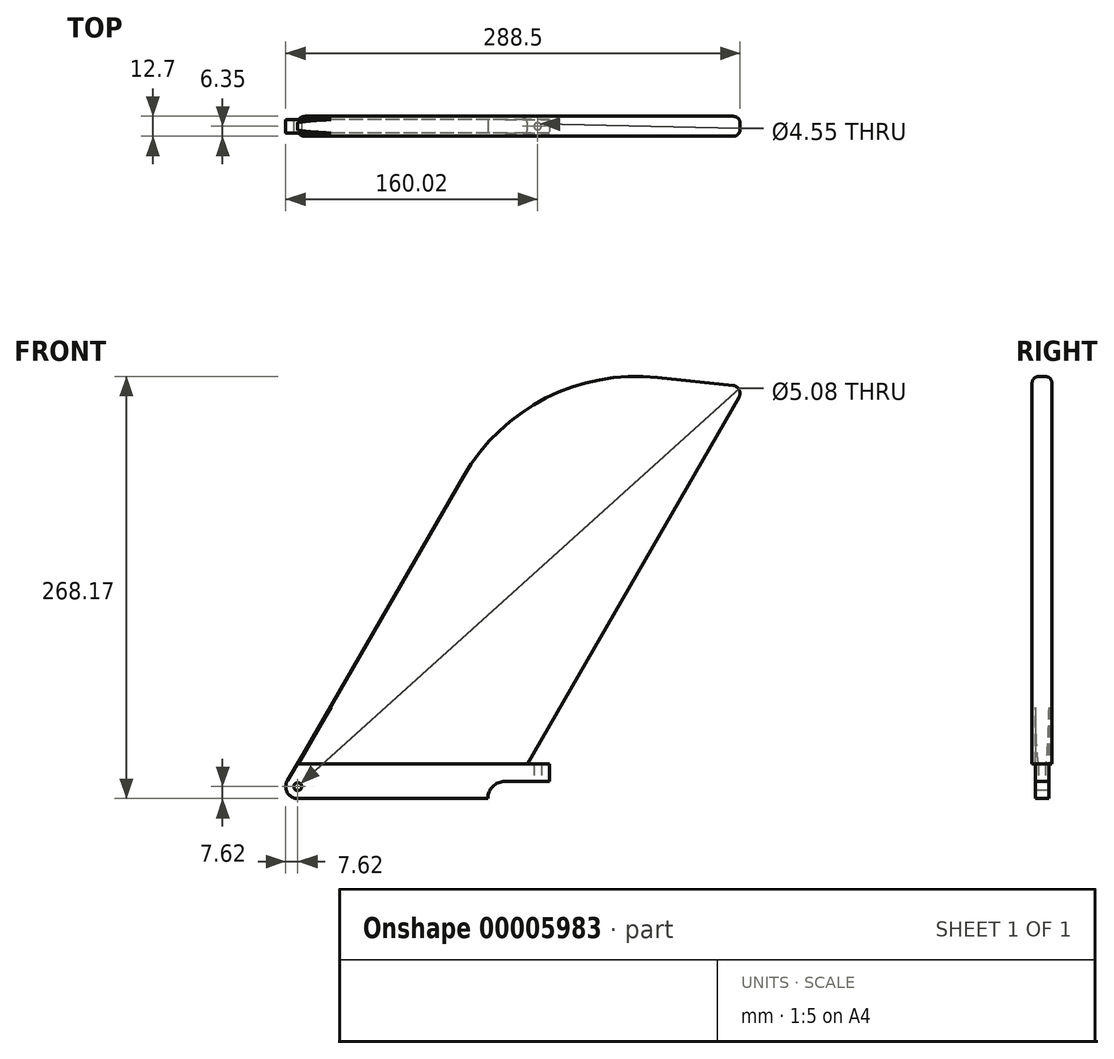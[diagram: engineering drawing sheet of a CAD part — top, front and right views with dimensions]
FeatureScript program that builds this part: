
annotation { "Feature Type Name" : "Feature", "Feature Type Description" : "" }
export const myFeature = defineFeature(function(context is Context, id is Id, definition is map)
    precondition{}
    {
        {
            var Q0;
            Q0=qCreatedBy(makeId("Top.planeOp"),FACE);
            var sketch = newSketch(context, id + "F0", { "sketchPlane" : qUnion([Q0])});
            skLineSegment(sketch, "E0.rect.bottom", {"start": v(83.82, 4.25) * mm, "end": v(-83.82, 4.25) * mm});
            skLineSegment(sketch, "E0.rect.top", {"start": v(83.82, -4.25) * mm, "end": v(-83.82, -4.25) * mm});
            skLineSegment(sketch, "E0.rect.left", {"start": v(83.82, 4.25) * mm, "end": v(83.82, -4.25) * mm});
            skLineSegment(sketch, "E0.rect.right", {"start": v(-83.82, 4.25) * mm, "end": v(-83.82, -4.25) * mm});
            skPoint(sketch, "E0.rect.middle", {"position": v(0, 0) * mm});
            skSolve(sketch);
        }
        {
            var Q0;
            Q0 = qSketchRegion(id + "F0", true);
            extrude(context, id + "F1", {"entities" : qUnion([Q0]), "depth" : 22.1 * mm});
        }
        {
            var Q0;
            Q0=qCreatedBy(makeId("Front.planeOp"),FACE);
            var sketch = newSketch(context, id + "F2", { "sketchPlane" : qUnion([Q0])});
            skArc(sketch, "E1", {"start": v(55.37, 10.85) * mm, "mid": v(47.7, 7.67) * mm, "end": v(44.52, 0) * mm});
            skLineSegment(sketch, "E2.0", {"start": v(83.82, 22.1) * mm, "end": v(83.82, 0) * mm});
            skLineSegment(sketch, "E3", {"start": v(55.37, 10.85) * mm, "end": v(83.82, 10.85) * mm});
            skLineSegment(sketch, "E4.0", {"start": v(83.82, 0) * mm, "end": v(-83.82, 0) * mm});
            skSolve(sketch);
        }
        {
            var Q0;
            Q0 = qSketchRegion(id + "F2", true);
            extrude(context, id + "F3", {"entities" : qUnion([Q0]), "operationType" : NewBodyOperationType.REMOVE, "endBound" : BoundingType.SYMMETRIC, "oppositeDirection" : true, "depth" : 25.4 * mm});
        }
        {
            var Q0;
            Q0=qCreatedBy(makeId("Front.planeOp"),FACE);
            var sketch = newSketch(context, id + "F4", { "sketchPlane" : qUnion([Q0])});
            skCircle(sketch, "E5", {"center": v(-76.2, 7.62) * mm, "radius": 2.54 * mm});
            skLineSegment(sketch, "E6.0", {"start": v(-83.82, 22.1) * mm, "end": v(-83.82, 0) * mm});
            skLineSegment(sketch, "E7.0", {"start": v(44.52, 0) * mm, "end": v(-83.82, 0) * mm});
            skSolve(sketch);
        }
        {
            var Q0;
            Q0=makeQuery(id+"F4.imprint","IMPRINT",FACE,{"disambiguationData":[TD([[makeQuery(id+"F4.imprint","IMPRINT",EDGE,{"derivedFrom":sQuery(id+"F4.wireOp",EDGE,"E5")}),1.0]])]});
            extrude(context, id + "F5", {"entities" : qUnion([Q0]), "operationType" : NewBodyOperationType.REMOVE, "endBound" : BoundingType.SYMMETRIC, "oppositeDirection" : true, "depth" : 25.4 * mm});
        }
        {
            var Q0;
            Q0=qCreatedBy(makeId("Front.planeOp"),FACE);
            var sketch = newSketch(context, id + "F6", { "sketchPlane" : qUnion([Q0])});
            skCircle(sketch, "E8.0", {"center": v(-76.2, 7.62) * mm, "radius": 2.54 * mm});
            skLineSegment(sketch, "E9.0", {"start": v(44.52, 0) * mm, "end": v(-83.82, 0) * mm});
            skLineSegment(sketch, "E10.0", {"start": v(-83.82, 22.1) * mm, "end": v(-83.82, 0) * mm});
            skArc(sketch, "E11", {"start": v(-82.74, 11.53) * mm, "mid": v(-82.83, 3.86) * mm, "end": v(-76.2, 0) * mm});
            skLineSegment(sketch, "E12", {"start": v(-76.32, 22.28) * mm, "end": v(-82.74, 11.53) * mm});
            skLineSegment(sketch, "E13", {"start": v(-76.32, 22.28) * mm, "end": v(-83.82, 22.1) * mm});
            skLineSegment(sketch, "E14", {"start": v(-83.82, 0) * mm, "end": v(-76.2, 0) * mm});
            skSolve(sketch);
        }
        {
            var Q0;
            Q0 = qSketchRegion(id + "F6", true);
            extrude(context, id + "F7", {"entities" : qUnion([Q0]), "operationType" : NewBodyOperationType.REMOVE, "endBound" : BoundingType.SYMMETRIC, "oppositeDirection" : true, "depth" : 25.4 * mm});
        }
        {
            var Q0;
            Q0=makeQuery(id+"F3.boolean.opBoolean","COPY",FACE,{"derivedFrom":makeQuery(id+"F3.opExtrude","SWEPT_FACE",FACE,{"disambiguationData":[OSD([sQuery(id+"F2.wireOp",EDGE,"E3")])]})});
            var sketch = newSketch(context, id + "F8", { "sketchPlane" : qUnion([Q0])});
            skCircle(sketch, "E15", {"center": v(76.2, 0) * mm, "radius": 2.27 * mm});
            skSolve(sketch);
        }
        {
            var Q0;
            Q0 = qSketchRegion(id + "F8", true);
            extrude(context, id + "F9", {"entities" : qUnion([Q0]), "operationType" : NewBodyOperationType.REMOVE, "oppositeDirection" : true, "depth" : 25.4 * mm});
        }
        {
            var Q0;
            Q0=qCreatedBy(makeId("Front.planeOp"),FACE);
            var sketch = newSketch(context, id + "F10", { "sketchPlane" : qUnion([Q0])});
            skPoint(sketch, "E16.0", {"position": v(-76.43, 22.1) * mm});
            skLineSegment(sketch, "E17.0", {"start": v(83.82, 22.1) * mm, "end": v(-76.43, 22.1) * mm});
            skLineSegment(sketch, "E18", {"start": v(-76.43, 22.1) * mm, "end": v(70.22, 276.1) * mm});
            skLineSegment(sketch, "E19", {"start": v(70.22, 276.1) * mm, "end": v(207.91, 261.63) * mm});
            skLineSegment(sketch, "E20", {"start": v(207.91, 261.63) * mm, "end": v(69.62, 22.1) * mm});
            skSolve(sketch);
        }
        {
            var Q0;
            Q0 = qSketchRegion(id + "F10", true);
            extrude(context, id + "F11", {"entities" : qUnion([Q0]), "operationType" : NewBodyOperationType.ADD, "endBound" : BoundingType.SYMMETRIC, "depth" : 12.7 * mm});
        }
        {
            var Q0;
            Q0=makeQuery(id+"F11.opExtrude","SWEPT_EDGE",EDGE,{"disambiguationData":[OSD([sQuery(id+"F10.wireOp",EDGE,"E18"),sQuery(id+"F10.wireOp",EDGE,"E19")])]});
            fillet(context, id + "F12", {"entities" : qUnion([Q0]), "radius" : 127 * mm, "tangentPropagation" : true, "allowEdgeOverflow" : false});
        }
        {
            var Q0;
            Q0=makeQuery(id+"F11.opExtrude","SWEPT_EDGE",EDGE,{"disambiguationData":[OSD([sQuery(id+"F10.wireOp",EDGE,"E19"),sQuery(id+"F10.wireOp",EDGE,"E20")])]});
            fillet(context, id + "F13", {"entities" : qUnion([Q0]), "radius" : 5.08 * mm, "tangentPropagation" : true, "allowEdgeOverflow" : false});
        }
        {
            var Q0;
            Q0=makeQuery(id+"F11.opExtrude","CAP_EDGE",EDGE,{"disambiguationData":[OSD([sQuery(id+"F10.wireOp",EDGE,"E18")])],"isStart":true});
            var Q1;
            Q1=makeQuery(id+"F11.opExtrude","CAP_EDGE",EDGE,{"disambiguationData":[OSD([sQuery(id+"F10.wireOp",EDGE,"E18")])],"isStart":false});
            fillet(context, id + "F14", {"entities" : qUnion([Q0, Q1]), "radius" : 4.32 * mm, "tangentPropagation" : true, "allowEdgeOverflow" : false});
        }
    });
